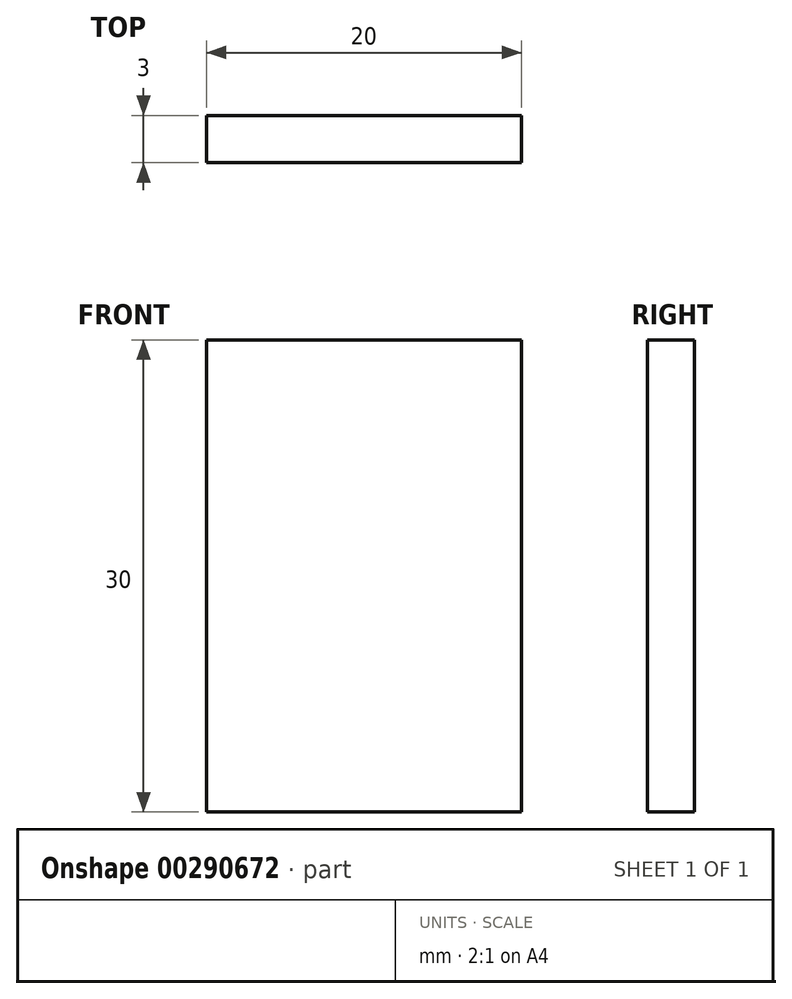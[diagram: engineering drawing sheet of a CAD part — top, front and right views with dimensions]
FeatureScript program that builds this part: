
annotation { "Feature Type Name" : "Feature", "Feature Type Description" : "" }
export const myFeature = defineFeature(function(context is Context, id is Id, definition is map)
    precondition{}
    {
        {
            var Q0;
            Q0=qCreatedBy(makeId("Front.planeOp"),FACE);
            var sketch = newSketch(context, id + "F0", { "sketchPlane" : qUnion([Q0])});
            skLineSegment(sketch, "E0", {"start": v(0, 0) * mm, "end": v(20, 0) * mm});
            skLineSegment(sketch, "E1", {"start": v(20, 0) * mm, "end": v(20, 30) * mm});
            skLineSegment(sketch, "E2", {"start": v(20, 30) * mm, "end": v(0, 30) * mm});
            skLineSegment(sketch, "E3", {"start": v(0, 30) * mm, "end": v(0, 0) * mm});
            skLineSegment(sketch, "E4", {"start": v(20, 15) * mm, "end": v(0, 15) * mm, "construction": true});
            skSolve(sketch);
        }
        {
            var Q0;
            Q0=makeQuery(id+"F0.imprint","IMPRINT",FACE,{"disambiguationData":[TD([[makeQuery(id+"F0.imprint","IMPRINT",EDGE,{"derivedFrom":sQuery(id+"F0.wireOp",EDGE,"E0")}),1.0]])]});
            extrude(context, id + "F1", {"entities" : qUnion([Q0]), "depth" : 3 * mm});
        }
    });
